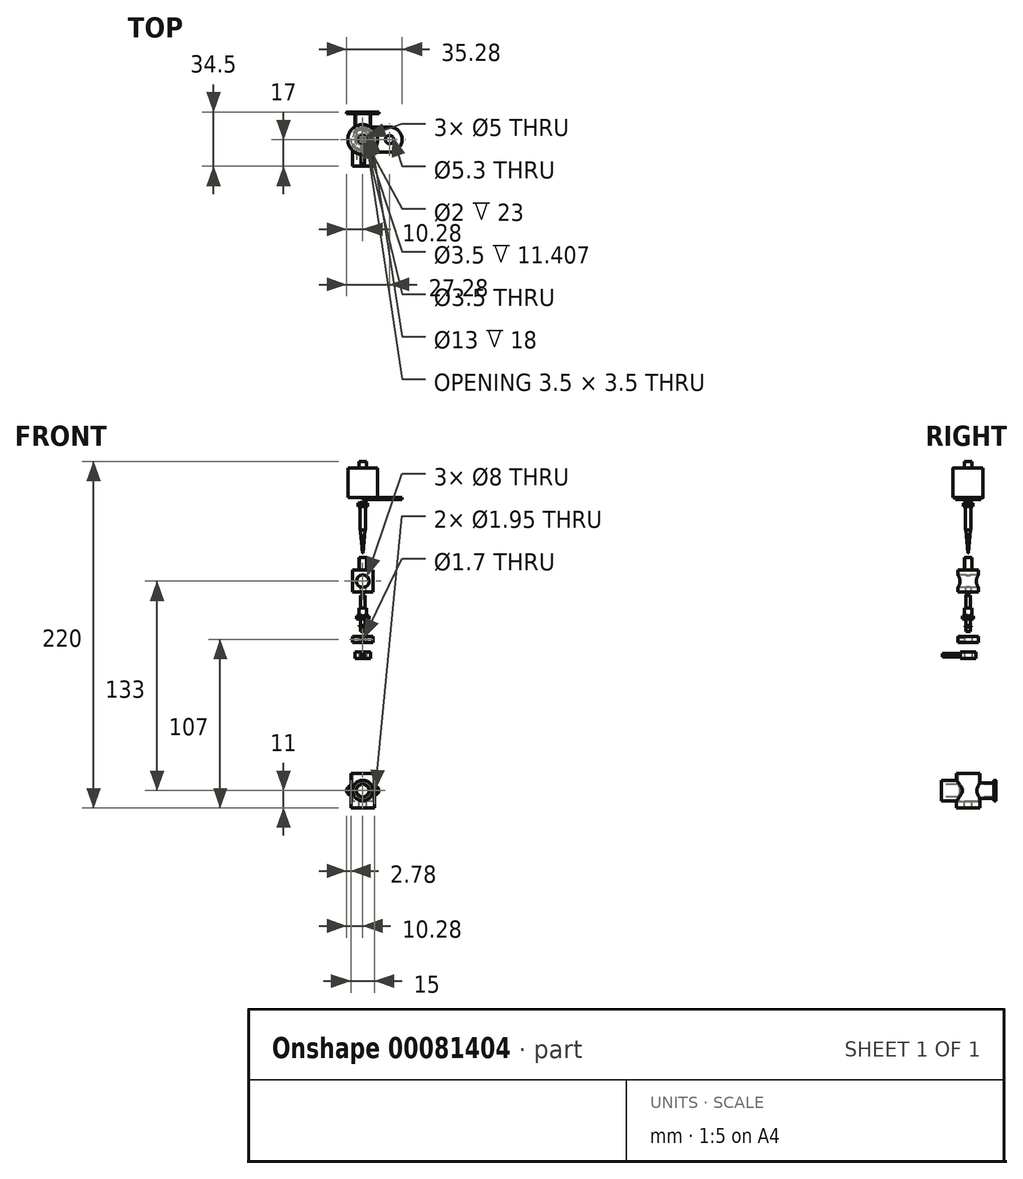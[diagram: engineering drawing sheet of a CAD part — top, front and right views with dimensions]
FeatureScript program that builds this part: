
annotation { "Feature Type Name" : "Feature", "Feature Type Description" : "" }
export const myFeature = defineFeature(function(context is Context, id is Id, definition is map)
    precondition{}
    {
        {
            var Q0;
            Q0=qCreatedBy(makeId("Front.planeOp"),FACE);
            var sketch = newSketch(context, id + "F0", { "sketchPlane" : qUnion([Q0])});
            skLineSegment(sketch, "E0", {"start": v(0, 0) * mm, "end": v(0, 3) * mm});
            skLineSegment(sketch, "E1", {"start": v(0, 3) * mm, "end": v(1.5, 3) * mm});
            skLineSegment(sketch, "E2", {"start": v(0, 3) * mm, "end": v(0, 4) * mm});
            skLineSegment(sketch, "E3", {"start": v(0, 4) * mm, "end": v(2.5, 4) * mm});
            skLineSegment(sketch, "E4", {"start": v(2.5, 4) * mm, "end": v(1.5, 3) * mm});
            skLineSegment(sketch, "E5", {"start": v(1.5, 3) * mm, "end": v(1.5, 0) * mm});
            skLineSegment(sketch, "E6", {"start": v(1.5, 0) * mm, "end": v(0, 0) * mm});
            skLineSegment(sketch, "E7", {"start": v(0, 4) * mm, "end": v(0, 8) * mm});
            skLineSegment(sketch, "E8", {"start": v(0, 8) * mm, "end": v(1.5, 8) * mm});
            skLineSegment(sketch, "E9", {"start": v(1.5, 8) * mm, "end": v(1.5, 4) * mm});
            skLineSegment(sketch, "E10", {"start": v(0, 0) * mm, "end": v(1, 0) * mm});
            skLineSegment(sketch, "E11", {"start": v(1, 0) * mm, "end": v(1, 3) * mm});
            skLineSegment(sketch, "E12", {"start": v(1, 3) * mm, "end": v(1, 4) * mm});
            skLineSegment(sketch, "E13", {"start": v(1, 4) * mm, "end": v(1, 8) * mm});
            skSolve(sketch);
        }
        {
            var Q0;
            {var subQ0=sQuery(id+"F0.wireOp",EDGE,"E9");Q0=makeQuery(id+"F0.imprint","IMPRINT",FACE,{"disambiguationData":[TD([[makeQuery(id+"F0.imprint","IMPRINT",EDGE,{"derivedFrom":subQ0}),-1.0]])]});}
            var Q1;
            {var subQ0=sQuery(id+"F0.wireOp",EDGE,"E4");Q1=makeQuery(id+"F0.imprint","IMPRINT",FACE,{"disambiguationData":[TD([[makeQuery(id+"F0.imprint","IMPRINT",EDGE,{"derivedFrom":subQ0}),-1.0]])]});}
            var Q2;
            {var subQ0=sQuery(id+"F0.wireOp",EDGE,"E5");Q2=makeQuery(id+"F0.imprint","IMPRINT",FACE,{"disambiguationData":[TD([[makeQuery(id+"F0.imprint","IMPRINT",EDGE,{"derivedFrom":subQ0}),-1.0]])]});}
            var Q3;
            Q3=sQuery(id+"F0.wireOp",EDGE,"E7");
            revolve(context, id + "F1", {"entities" : qUnion([Q0, Q1, Q2]), "axis" : qUnion([Q3]), "revolveType" : RevolveType.FULL});
        }
        {
            var Q0;
            Q0=makeQuery(id+"F1.opRevolve","SWEPT_FACE",FACE,{"disambiguationData":[OSD([sQuery(id+"F0.wireOp",EDGE,"E8")])]});
            var sketch = newSketch(context, id + "F2", { "sketchPlane" : qUnion([Q0])});
            skCircle(sketch, "E14.cCircle", {"center": v(0, 0) * mm, "radius": 4.04 * mm, "construction": true});
            skLineSegment(sketch, "E14.0", {"start": v(4.04, 0) * mm, "end": v(2.02, -3.5) * mm});
            skLineSegment(sketch, "E14.1", {"start": v(2.02, -3.5) * mm, "end": v(-2.02, -3.5) * mm});
            skLineSegment(sketch, "E14.2", {"start": v(-2.02, -3.5) * mm, "end": v(-4.04, 0) * mm});
            skLineSegment(sketch, "E14.3", {"start": v(-4.04, 0) * mm, "end": v(-2.02, 3.5) * mm});
            skLineSegment(sketch, "E14.4", {"start": v(-2.02, 3.5) * mm, "end": v(2.02, 3.5) * mm});
            skLineSegment(sketch, "E14.5", {"start": v(2.02, 3.5) * mm, "end": v(4.04, 0) * mm});
            skCircle(sketch, "E15", {"center": v(0, 0) * mm, "radius": 1 * mm});
            skSolve(sketch);
        }
        {
            var Q0;
            Q0 = qSketchRegion(id + "F2", true);
            extrude(context, id + "F3", {"entities" : qUnion([Q0]), "operationType" : NewBodyOperationType.ADD, "depth" : 2 * mm});
        }
        {
            var Q0;
            Q0=makeQuery(id+"F3.opExtrude","CAP_FACE",FACE,{"disambiguationData":[OSD([sQuery(id+"F2.wireOp",EDGE,"E14.0"),sQuery(id+"F2.wireOp",EDGE,"E14.1"),sQuery(id+"F2.wireOp",EDGE,"E14.2"),sQuery(id+"F2.wireOp",EDGE,"E14.3"),sQuery(id+"F2.wireOp",EDGE,"E14.4"),sQuery(id+"F2.wireOp",EDGE,"E14.5"),sQuery(id+"F2.wireOp",EDGE,"E15")])],"isStart":false});
            var sketch = newSketch(context, id + "F4", { "sketchPlane" : qUnion([Q0])});
            skCircle(sketch, "E16", {"center": v(0, 0) * mm, "radius": 1 * mm});
            skCircle(sketch, "E17", {"center": v(0, 0) * mm, "radius": 2.5 * mm});
            skSolve(sketch);
        }
        {
            var Q0;
            Q0 = qSketchRegion(id + "F4", true);
            extrude(context, id + "F5", {"entities" : qUnion([Q0]), "operationType" : NewBodyOperationType.ADD, "depth" : 5 * mm});
        }
        {
            var Q0;
            Q0=makeQuery(id+"F5.opExtrude","CAP_FACE",FACE,{"disambiguationData":[OSD([sQuery(id+"F4.wireOp",EDGE,"E16"),sQuery(id+"F4.wireOp",EDGE,"E17")])],"isStart":false});
            var sketch = newSketch(context, id + "F6", { "sketchPlane" : qUnion([Q0])});
            skCircle(sketch, "E18", {"center": v(0, 0) * mm, "radius": 1 * mm});
            skCircle(sketch, "E19", {"center": v(0, 0) * mm, "radius": 1.5 * mm});
            skSolve(sketch);
        }
        {
            var Q0;
            Q0 = qSketchRegion(id + "F6", true);
            extrude(context, id + "F7", {"entities" : qUnion([Q0]), "operationType" : NewBodyOperationType.ADD, "depth" : 8 * mm});
        }
        {
            var Q0;
            Q0=makeQuery(id+"F1.opRevolve","SWEPT_BODY",BODY,{"disambiguationData":[OSD([sQuery(id+"F0.wireOp",EDGE,"E3"),sQuery(id+"F0.wireOp",EDGE,"E4"),sQuery(id+"F0.wireOp",EDGE,"E5"),sQuery(id+"F0.wireOp",EDGE,"E6"),sQuery(id+"F0.wireOp",EDGE,"E8"),sQuery(id+"F0.wireOp",EDGE,"E9"),sQuery(id+"F0.wireOp",EDGE,"E11"),sQuery(id+"F0.wireOp",EDGE,"E12"),sQuery(id+"F0.wireOp",EDGE,"E13")])]});
            transform(context, id + "F8", {"entities" : qUnion([Q0]), "transformType" : TransformType.TRANSLATION_3D, "dx" : 0 * mm, "dy" : 0 * mm, "dz" : 100 * mm, "makeCopy" : false});
        }
        {
            var Q0;
            Q0=qCreatedBy(makeId("Top.planeOp"),FACE);
            var sketch = newSketch(context, id + "F9", { "sketchPlane" : qUnion([Q0])});
            skCircle(sketch, "E20", {"center": v(0, 0) * mm, "radius": 6.5 * mm});
            skCircle(sketch, "E21", {"center": v(0, 0) * mm, "radius": 1.75 * mm});
            skSolve(sketch);
        }
        {
            var Q0;
            Q0 = qSketchRegion(id + "F9", true);
            extrude(context, id + "F10", {"entities" : qUnion([Q0]), "depth" : 14 * mm});
        }
        {
            var Q0;
            Q0=makeQuery(id+"F10.opExtrude","CAP_FACE",FACE,{"disambiguationData":[OSD([sQuery(id+"F9.wireOp",EDGE,"E20"),sQuery(id+"F9.wireOp",EDGE,"E21")])],"isStart":false});
            var sketch = newSketch(context, id + "F11", { "sketchPlane" : qUnion([Q0])});
            skCircle(sketch, "E22", {"center": v(0, 0) * mm, "radius": 1.75 * mm});
            skCircle(sketch, "E23", {"center": v(0, 0) * mm, "radius": 2.5 * mm});
            skSolve(sketch);
        }
        {
            var Q0;
            Q0 = qSketchRegion(id + "F11", true);
            extrude(context, id + "F12", {"entities" : qUnion([Q0]), "operationType" : NewBodyOperationType.ADD, "depth" : 8 * mm});
        }
        {
            var Q0;
            Q0=qCreatedBy(makeId("Front.planeOp"),FACE);
            var sketch = newSketch(context, id + "F13", { "sketchPlane" : qUnion([Q0])});
            skLineSegment(sketch, "E24", {"start": v(0, 0) * mm, "end": v(0, 7) * mm});
            skCircle(sketch, "E25", {"center": v(0, 7) * mm, "radius": 4 * mm});
            skSolve(sketch);
        }
        {
            var Q0;
            Q0 = qSketchRegion(id + "F13", true);
            extrude(context, id + "F14", {"entities" : qUnion([Q0]), "operationType" : NewBodyOperationType.REMOVE, "endBound" : BoundingType.SYMMETRIC, "oppositeDirection" : true, "depth" : 25 * mm});
        }
        {
            var Q0;
            Q0=makeQuery(id+"F10.opExtrude","SWEPT_BODY",BODY,{"disambiguationData":[OSD([sQuery(id+"F9.wireOp",EDGE,"E20"),sQuery(id+"F9.wireOp",EDGE,"E21")])]});
            transform(context, id + "F15", {"entities" : qUnion([Q0]), "transformType" : TransformType.TRANSLATION_3D, "dx" : 0 * mm, "dy" : 0 * mm, "dz" : 125 * mm, "makeCopy" : false});
        }
        {
            var Q0;
            Q0=qCreatedBy(makeId("Top.planeOp"),FACE);
            var sketch = newSketch(context, id + "F16", { "sketchPlane" : qUnion([Q0])});
            skCircle(sketch, "E26", {"center": v(0, 0) * mm, "radius": 6.5 * mm});
            skCircle(sketch, "E27", {"center": v(0, 0) * mm, "radius": 2.5 * mm});
            skSolve(sketch);
        }
        {
            var Q0;
            Q0 = qSketchRegion(id + "F16", true);
            extrude(context, id + "F17", {"entities" : qUnion([Q0]), "endBound" : BoundingType.SYMMETRIC, "depth" : 4 * mm});
        }
        {
            var Q0;
            Q0=qCreatedBy(makeId("Front.planeOp"),FACE);
            var sketch = newSketch(context, id + "F18", { "sketchPlane" : qUnion([Q0])});
            skCircle(sketch, "E28", {"center": v(0, 0) * mm, "radius": 0.85 * mm});
            skSolve(sketch);
        }
        {
            var Q0;
            Q0 = qSketchRegion(id + "F18", true);
            extrude(context, id + "F19", {"entities" : qUnion([Q0]), "operationType" : NewBodyOperationType.REMOVE, "depth" : 25 * mm});
        }
        {
            var Q0;
            Q0=makeQuery(id+"F17.opExtrude","SWEPT_BODY",BODY,{"disambiguationData":[OSD([sQuery(id+"F16.wireOp",EDGE,"E26"),sQuery(id+"F16.wireOp",EDGE,"E27")])]});
            transform(context, id + "F20", {"entities" : qUnion([Q0]), "transformType" : TransformType.TRANSLATION_3D, "dx" : 0 * mm, "dy" : 0 * mm, "dz" : 95 * mm, "makeCopy" : false});
        }
        {
            var Q0;
            Q0=qCreatedBy(makeId("Top.planeOp"),FACE);
            var sketch = newSketch(context, id + "F21", { "sketchPlane" : qUnion([Q0])});
            skCircle(sketch, "E29", {"center": v(0, 0) * mm, "radius": 5 * mm});
            skCircle(sketch, "E30", {"center": v(0, 0) * mm, "radius": 2.5 * mm});
            skSolve(sketch);
        }
        {
            var Q0;
            Q0 = qSketchRegion(id + "F21", true);
            extrude(context, id + "F22", {"entities" : qUnion([Q0]), "endBound" : BoundingType.SYMMETRIC, "depth" : 4 * mm});
        }
        {
            var Q0;
            Q0=qCreatedBy(makeId("Front.planeOp"),FACE);
            var sketch = newSketch(context, id + "F23", { "sketchPlane" : qUnion([Q0])});
            skCircle(sketch, "E31", {"center": v(0, 0) * mm, "radius": 1.1 * mm});
            skSolve(sketch);
        }
        {
            var Q0;
            Q0 = qSketchRegion(id + "F23", true);
            extrude(context, id + "F24", {"entities" : qUnion([Q0]), "operationType" : NewBodyOperationType.ADD, "depth" : 16.5 * mm});
        }
        {
            var Q0;
            Q0=makeQuery(id+"F22.opExtrude","CAP_FACE",FACE,{"disambiguationData":[OSD([sQuery(id+"F21.wireOp",EDGE,"E29"),sQuery(id+"F21.wireOp",EDGE,"E30")])],"isStart":false});
            var sketch = newSketch(context, id + "F25", { "sketchPlane" : qUnion([Q0])});
            skSolve(sketch);
        }
        {
            var Q0;
            Q0 = qSketchRegion(id + "F25", true);
            var Q1;
            Q1=makeQuery(id+"F25.imprint","IMPRINT",FACE,{"disambiguationData":[TD([[makeQuery(id+"F25.imprint","IMPRINT",EDGE,{"derivedFrom":makeQuery(id+"F22.opExtrude","CAP_EDGE",EDGE,{"disambiguationData":[OSD([sQuery(id+"F21.wireOp",EDGE,"E30")])],"isStart":false})}),1.0]])]});
            extrude(context, id + "F26", {"entities" : qUnion([Q0, Q1]), "operationType" : NewBodyOperationType.REMOVE, "oppositeDirection" : true, "depth" : 25 * mm});
        }
        {
            var Q0;
            Q0=makeQuery(id+"F22.opExtrude","SWEPT_BODY",BODY,{"disambiguationData":[OSD([sQuery(id+"F21.wireOp",EDGE,"E29"),sQuery(id+"F21.wireOp",EDGE,"E30")])]});
            transform(context, id + "F27", {"entities" : qUnion([Q0]), "transformType" : TransformType.TRANSLATION_3D, "dx" : 0 * mm, "dy" : 0 * mm, "dz" : 85 * mm, "makeCopy" : false});
        }
        {
            var Q0;
            Q0=qCreatedBy(makeId("Front.planeOp"),FACE);
            var sketch = newSketch(context, id + "F28", { "sketchPlane" : qUnion([Q0])});
            skLineSegment(sketch, "E32", {"start": v(0, 0) * mm, "end": v(0, 14.5) * mm});
            skLineSegment(sketch, "E33", {"start": v(0, 14.5) * mm, "end": v(1.8, 14.5) * mm});
            skLineSegment(sketch, "E34", {"start": v(1.8, 14.5) * mm, "end": v(1.8, 29.5) * mm});
            skLineSegment(sketch, "E35", {"start": v(1.8, 29.5) * mm, "end": v(0, 29.5) * mm});
            skLineSegment(sketch, "E36", {"start": v(0, 29.5) * mm, "end": v(3, 29.5) * mm});
            skLineSegment(sketch, "E37", {"start": v(3, 29.5) * mm, "end": v(3, 31.5) * mm});
            skLineSegment(sketch, "E38", {"start": v(3, 31.5) * mm, "end": v(0, 31.5) * mm});
            skLineSegment(sketch, "E39", {"start": v(0, 29.5) * mm, "end": v(0, 31.5) * mm});
            skLineSegment(sketch, "E40", {"start": v(0, 31.5) * mm, "end": v(0, 32) * mm});
            skLineSegment(sketch, "E41", {"start": v(0, 31.5) * mm, "end": v(-3, 31.5) * mm});
            skArc(sketch, "E42", {"start": v(3, 31.5) * mm, "mid": v(1.52, 31.86) * mm, "end": v(0, 32) * mm});
            skLineSegment(sketch, "E43", {"start": v(0, 0) * mm, "end": v(0.12, 0) * mm});
            skLineSegment(sketch, "E44", {"start": v(0, 14.5) * mm, "end": v(1.5, 14.5) * mm});
            skLineSegment(sketch, "E45", {"start": v(1.5, 14.5) * mm, "end": v(0.13, 0) * mm});
            skLineSegment(sketch, "E46", {"start": v(0, 14.5) * mm, "end": v(0, 29.5) * mm});
            skSolve(sketch);
        }
        {
            var Q0;
            Q0 = qSketchRegion(id + "F28", true);
            var Q1;
            Q1=sQuery(id+"F28.wireOp",EDGE,"E46");
            revolve(context, id + "F29", {"entities" : qUnion([Q0]), "axis" : qUnion([Q1]), "revolveType" : RevolveType.FULL});
        }
        {
            var Q0;
            Q0=makeQuery(id+"F29.opRevolve","SWEPT_BODY",BODY,{"disambiguationData":[OSD([sQuery(id+"F28.wireOp",EDGE,"E32"),sQuery(id+"F28.wireOp",EDGE,"E33"),sQuery(id+"F28.wireOp",EDGE,"E34"),sQuery(id+"F28.wireOp",EDGE,"E36"),sQuery(id+"F28.wireOp",EDGE,"E37"),sQuery(id+"F28.wireOp",EDGE,"E39"),sQuery(id+"F28.wireOp",EDGE,"E40"),sQuery(id+"F28.wireOp",EDGE,"E42"),sQuery(id+"F28.wireOp",EDGE,"E43"),sQuery(id+"F28.wireOp",EDGE,"E45"),sQuery(id+"F28.wireOp",EDGE,"E46")])]});
            transform(context, id + "F30", {"entities" : qUnion([Q0]), "transformType" : TransformType.TRANSLATION_3D, "dx" : 0 * mm, "dy" : 0 * mm, "dz" : 150 * mm, "makeCopy" : false});
        }
        {
            var Q0;
            Q0=qCreatedBy(makeId("Top.planeOp"),FACE);
            var sketch = newSketch(context, id + "F31", { "sketchPlane" : qUnion([Q0])});
            skCircle(sketch, "E47", {"center": v(0, 0) * mm, "radius": 9.5 * mm});
            skCircle(sketch, "E48", {"center": v(0, 0) * mm, "radius": 2.5 * mm});
            skSolve(sketch);
        }
        {
            var Q0;
            Q0 = qSketchRegion(id + "F31", true);
            var Q1;
            Q1=makeQuery(id+"F31.imprint","IMPRINT",FACE,{"disambiguationData":[TD([[makeQuery(id+"F31.imprint","IMPRINT",EDGE,{"derivedFrom":sQuery(id+"F31.wireOp",EDGE,"E48")}),1.0]])]});
            extrude(context, id + "F32", {"entities" : qUnion([Q0, Q1]), "depth" : 19 * mm});
        }
        {
            var Q0;
            Q0=makeQuery(id+"F32.opExtrude","CAP_FACE",FACE,{"disambiguationData":[OSD([sQuery(id+"F31.wireOp",EDGE,"E47")])],"isStart":false});
            var sketch = newSketch(context, id + "F33", { "sketchPlane" : qUnion([Q0])});
            skCircle(sketch, "E49", {"center": v(0, 0) * mm, "radius": 2.5 * mm});
            skSolve(sketch);
        }
        {
            var Q0;
            Q0 = qSketchRegion(id + "F33", true);
            extrude(context, id + "F34", {"entities" : qUnion([Q0]), "operationType" : NewBodyOperationType.ADD, "depth" : 4 * mm});
        }
        {
            var Q0;
            Q0=makeQuery(id+"F32.opExtrude","CAP_FACE",FACE,{"disambiguationData":[OSD([sQuery(id+"F31.wireOp",EDGE,"E47")])],"isStart":true});
            var sketch = newSketch(context, id + "F35", { "sketchPlane" : qUnion([Q0])});
            skLineSegment(sketch, "E50", {"start": v(0, 0) * mm, "end": v(25, 0) * mm});
            skLineSegment(sketch, "E51", {"start": v(25, 0) * mm, "end": v(17, 0) * mm});
            skArc(sketch, "E52", {"start": v(17, -8) * mm, "mid": v(25, 0) * mm, "end": v(17, 8) * mm});
            skCircle(sketch, "E53", {"center": v(17, 0) * mm, "radius": 2.65 * mm});
            skLineSegment(sketch, "E54", {"start": v(17, 8) * mm, "end": v(0, 8) * mm});
            skLineSegment(sketch, "E55", {"start": v(0, 8) * mm, "end": v(0, 0) * mm});
            skLineSegment(sketch, "E56.MirrorCS", {"start": v(0, -8) * mm, "end": v(0, 0) * mm});
            skLineSegment(sketch, "E57.MirrorCS", {"start": v(17, -8) * mm, "end": v(0, -8) * mm});
            skSolve(sketch);
        }
        {
            var Q0;
            Q0 = qSketchRegion(id + "F35", true);
            extrude(context, id + "F36", {"entities" : qUnion([Q0]), "operationType" : NewBodyOperationType.ADD, "depth" : 1 * mm});
        }
        {
            var Q0;
            Q0=makeQuery(id+"F32.opExtrude","SWEPT_BODY",BODY,{"disambiguationData":[OSD([sQuery(id+"F31.wireOp",EDGE,"E47")])]});
            transform(context, id + "F37", {"entities" : qUnion([Q0]), "transformType" : TransformType.TRANSLATION_3D, "dx" : 0 * mm, "dy" : 0 * mm, "dz" : 185 * mm, "makeCopy" : false});
        }
        {
            var Q0;
            Q0=qCreatedBy(makeId("Top.planeOp"),FACE);
            var sketch = newSketch(context, id + "F38", { "sketchPlane" : qUnion([Q0])});
            skCircle(sketch, "E58", {"center": v(0, 0) * mm, "radius": 6.5 * mm});
            skCircle(sketch, "E59", {"center": v(0, 0) * mm, "radius": 7.5 * mm});
            skSolve(sketch);
        }
        {
            var Q0;
            Q0 = qSketchRegion(id + "F38", true);
            extrude(context, id + "F39", {"entities" : qUnion([Q0]), "endBound" : BoundingType.SYMMETRIC, "depth" : 20 * mm});
        }
        {
            var Q0;
            Q0=makeQuery(id+"F39.opExtrude","CAP_FACE",FACE,{"disambiguationData":[OSD([sQuery(id+"F38.wireOp",EDGE,"E58"),sQuery(id+"F38.wireOp",EDGE,"E59")])],"isStart":true});
            var sketch = newSketch(context, id + "F40", { "sketchPlane" : qUnion([Q0])});
            skCircle(sketch, "E60", {"center": v(0, 0) * mm, "radius": 7.5 * mm});
            skCircle(sketch, "E61", {"center": v(0, 0) * mm, "radius": 2.5 * mm});
            skSolve(sketch);
        }
        {
            var Q0;
            Q0 = qSketchRegion(id + "F40", true);
            extrude(context, id + "F41", {"entities" : qUnion([Q0]), "operationType" : NewBodyOperationType.ADD, "depth" : 2 * mm});
        }
        {
            var Q0;
            Q0=qCreatedBy(makeId("Front.planeOp"),FACE);
            var sketch = newSketch(context, id + "F42", { "sketchPlane" : qUnion([Q0])});
            skLineSegment(sketch, "E62", {"start": v(0, 0) * mm, "end": v(0, 10) * mm});
            skLineSegment(sketch, "E63", {"start": v(0, 10) * mm, "end": v(0, -1) * mm});
            skCircle(sketch, "E64", {"center": v(0, -1) * mm, "radius": 4 * mm});
            skCircle(sketch, "E65", {"center": v(0, -1) * mm, "radius": 5 * mm});
            skSolve(sketch);
        }
        {
            var Q0;
            Q0 = qSketchRegion(id + "F42", true);
            extrude(context, id + "F43", {"entities" : qUnion([Q0]), "operationType" : NewBodyOperationType.ADD, "oppositeDirection" : true, "depth" : 16.5 * mm});
        }
        {
            var Q0;
            Q0=makeQuery(id+"F43.opExtrude","CAP_FACE",FACE,{"disambiguationData":[OSD([sQuery(id+"F42.wireOp",EDGE,"E64"),sQuery(id+"F42.wireOp",EDGE,"E65")])],"isStart":false});
            var sketch = newSketch(context, id + "F44", { "sketchPlane" : qUnion([Q0])});
            skCircle(sketch, "E66", {"center": v(0, -1) * mm, "radius": 4 * mm});
            skArc(sketch, "E67", {"start": v(-3.26, -6.63) * mm, "mid": v(0, -7.5) * mm, "end": v(3.26, -6.63) * mm});
            skLineSegment(sketch, "E68", {"start": v(0, -1) * mm, "end": v(7.5, -1) * mm});
            skCircle(sketch, "E69", {"center": v(7.5, -1) * mm, "radius": 0.97 * mm});
            skLineSegment(sketch, "E70", {"start": v(0, -1) * mm, "end": v(0, 0) * mm});
            skCircle(sketch, "E71.MirrorC", {"center": v(-7.5, -1) * mm, "radius": 0.97 * mm});
            skArc(sketch, "E72", {"start": v(-8.88, 1.4) * mm, "mid": v(-10.27, -1) * mm, "end": v(-8.88, -3.4) * mm});
            skArc(sketch, "E73.MirrorC", {"start": v(8.88, 1.4) * mm, "mid": v(10.27, -1) * mm, "end": v(8.88, -3.4) * mm});
            skLineSegment(sketch, "E74", {"start": v(-3.26, 4.63) * mm, "end": v(-3.54, 5.12) * mm});
            skLineSegment(sketch, "E75", {"start": v(0, -1) * mm, "end": v(-1.82, -1) * mm});
            skLineSegment(sketch, "E76", {"start": v(-3.26, 4.63) * mm, "end": v(-8.88, 1.4) * mm});
            skLineSegment(sketch, "E77.MirrorCS", {"start": v(3.26, 4.63) * mm, "end": v(8.88, 1.4) * mm});
            skLineSegment(sketch, "E78.MirrorCS", {"start": v(-3.26, -6.63) * mm, "end": v(-8.88, -3.4) * mm});
            skLineSegment(sketch, "E79.MirrorCS", {"start": v(3.26, -6.63) * mm, "end": v(8.88, -3.4) * mm});
            skArc(sketch, "E80.trimOffspring", {"start": v(3.26, 4.63) * mm, "mid": v(0, 5.5) * mm, "end": v(-3.26, 4.63) * mm});
            skSolve(sketch);
        }
        {
            var Q0;
            Q0 = qSketchRegion(id + "F44", true);
            extrude(context, id + "F45", {"entities" : qUnion([Q0]), "operationType" : NewBodyOperationType.ADD, "depth" : 1 * mm});
        }
        {
            var Q0;
            Q0=makeQuery(id+"F43.opExtrude","CAP_FACE",FACE,{"disambiguationData":[OSD([sQuery(id+"F42.wireOp",EDGE,"E64"),sQuery(id+"F42.wireOp",EDGE,"E65")])],"isStart":true});
            var sketch = newSketch(context, id + "F46", { "sketchPlane" : qUnion([Q0])});
            skCircle(sketch, "E81", {"center": v(0, -1) * mm, "radius": 4 * mm});
            skCircle(sketch, "E82", {"center": v(0, -1) * mm, "radius": 6.5 * mm});
            skSolve(sketch);
        }
        {
            var Q0;
            Q0 = qSketchRegion(id + "F46", true);
            extrude(context, id + "F47", {"entities" : qUnion([Q0]), "operationType" : NewBodyOperationType.ADD, "depth" : 17 * mm});
        }
        {
            var Q0;
            Q0=makeQuery(id+"F47.opExtrude","CAP_FACE",FACE,{"disambiguationData":[OSD([sQuery(id+"F46.wireOp",EDGE,"E81"),sQuery(id+"F46.wireOp",EDGE,"E82")])],"isStart":false});
            var sketch = newSketch(context, id + "F48", { "sketchPlane" : qUnion([Q0])});
            skSolve(sketch);
        }
        {
            var Q0;
            Q0=makeQuery(id+"F48.imprint","IMPRINT",FACE,{"disambiguationData":[TD([[makeQuery(id+"F48.imprint","IMPRINT",EDGE,{"derivedFrom":makeQuery(id+"F47.opExtrude","CAP_EDGE",EDGE,{"disambiguationData":[OSD([sQuery(id+"F46.wireOp",EDGE,"E81")])],"isStart":false})}),1.0]])]});
            extrude(context, id + "F49", {"entities" : qUnion([Q0]), "operationType" : NewBodyOperationType.REMOVE, "oppositeDirection" : true, "depth" : 25 * mm});
        }
        {
            var Q0;
            Q0=makeQuery(id+"F39.opExtrude","CAP_FACE",FACE,{"disambiguationData":[OSD([sQuery(id+"F38.wireOp",EDGE,"E58"),sQuery(id+"F38.wireOp",EDGE,"E59")])],"isStart":false});
            var sketch = newSketch(context, id + "F50", { "sketchPlane" : qUnion([Q0])});
            skSolve(sketch);
        }
        {
            var Q0;
            Q0=makeQuery(id+"F50.imprint","IMPRINT",FACE,{"disambiguationData":[TD([[makeQuery(id+"F50.imprint","IMPRINT",EDGE,{"derivedFrom":makeQuery(id+"F39.opExtrude","CAP_EDGE",EDGE,{"disambiguationData":[OSD([sQuery(id+"F38.wireOp",EDGE,"E58")])],"isStart":false})}),1.0]])]});
            extrude(context, id + "F51", {"entities" : qUnion([Q0]), "operationType" : NewBodyOperationType.REMOVE, "oppositeDirection" : true, "depth" : 20 * mm});
        }
        {
            var Q0;
            Q0=makeQuery(id+"F41.opExtrude","CAP_FACE",FACE,{"disambiguationData":[OSD([sQuery(id+"F40.wireOp",EDGE,"E60"),sQuery(id+"F40.wireOp",EDGE,"E61")])],"isStart":true});
            var sketch = newSketch(context, id + "F52", { "sketchPlane" : qUnion([Q0])});
            skSolve(sketch);
        }
        {
            var Q0;
            Q0=makeQuery(id+"F52.imprint","IMPRINT",FACE,{"disambiguationData":[TD([[makeQuery(id+"F52.imprint","IMPRINT",EDGE,{"derivedFrom":makeQuery(id+"F41.opExtrude","CAP_EDGE",EDGE,{"disambiguationData":[OSD([sQuery(id+"F40.wireOp",EDGE,"E61")])],"isStart":true})}),1.0]])]});
            extrude(context, id + "F53", {"entities" : qUnion([Q0]), "operationType" : NewBodyOperationType.ADD, "depth" : 2 * mm});
        }
    });
